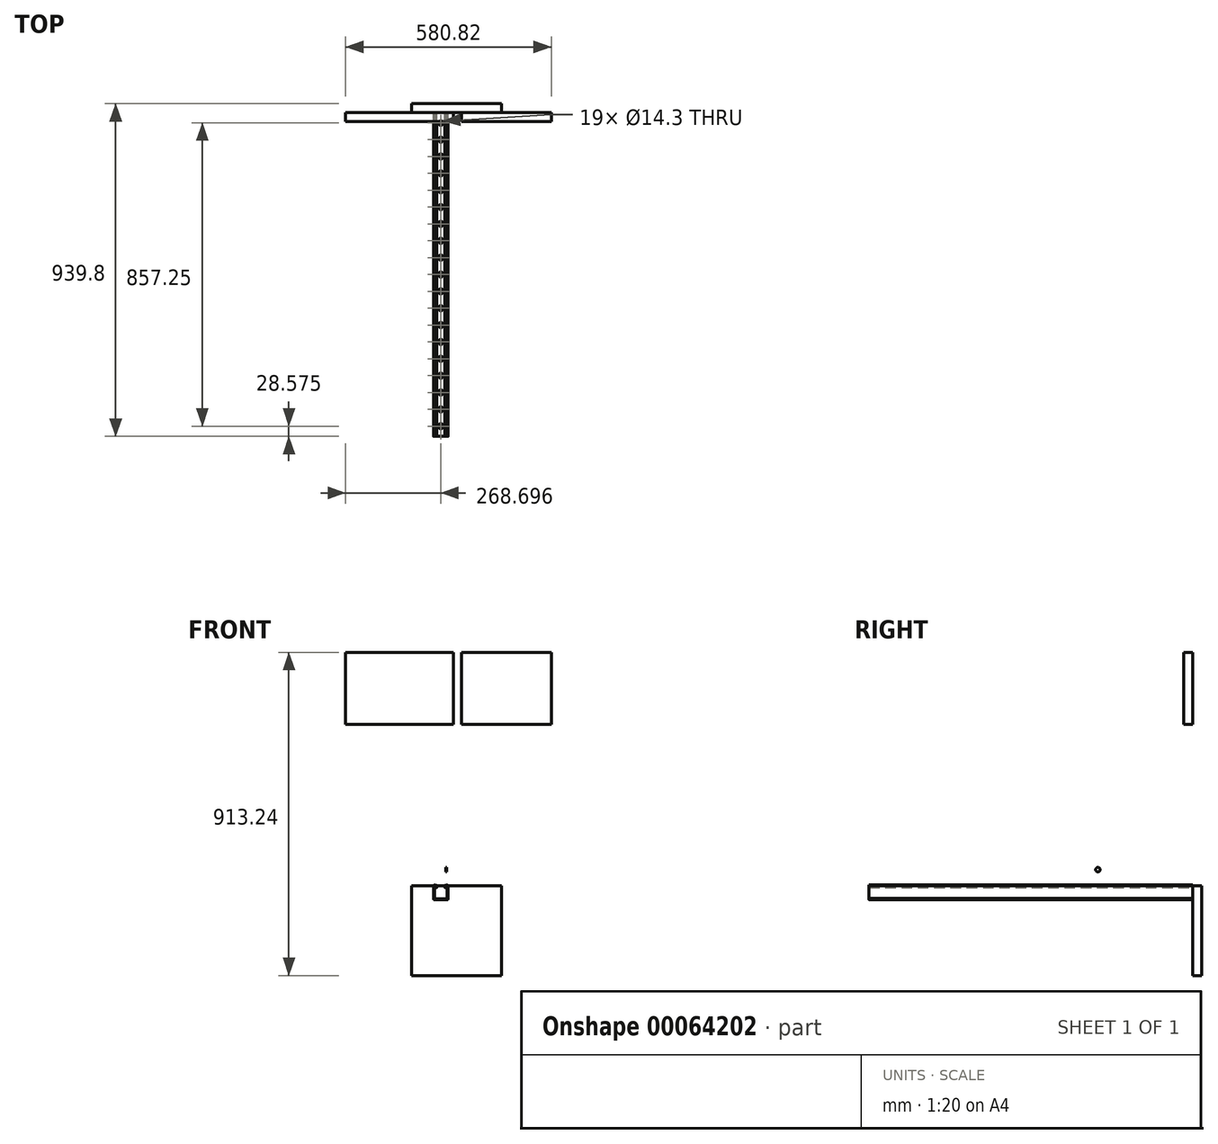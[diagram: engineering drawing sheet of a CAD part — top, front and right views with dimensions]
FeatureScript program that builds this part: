
annotation { "Feature Type Name" : "Feature", "Feature Type Description" : "" }
export const myFeature = defineFeature(function(context is Context, id is Id, definition is map)
    precondition{}
    {
        {
            var Q0;
            Q0=qCreatedBy(makeId("Front.planeOp"),FACE);
            var sketch = newSketch(context, id + "F0", { "sketchPlane" : qUnion([Q0])});
            skLineSegment(sketch, "E0.0", {"start": v(-47.01, 34.8) * mm, "end": v(-47.01, 32.45) * mm});
            skFitSpline(sketch, "E0.1", {"points": [v(-47.01, 32.45) * mm, v(-47.01, 31.71) * mm, v(-46.41, 31.12) * mm, v(-45.68, 31.12) * mm]});
            skFitSpline(sketch, "E0.2", {"points": [v(-45.68, 31.12) * mm, v(-44.94, 31.12) * mm, v(-44.34, 31.71) * mm, v(-44.34, 32.45) * mm]});
            skLineSegment(sketch, "E0.3", {"start": v(-44.34, 32.45) * mm, "end": v(-44.34, 34.8) * mm});
            skPoint(sketch, "E0.4", {"position": v(-43.55, 35.59) * mm});
            skPoint(sketch, "E0.5", {"position": v(-44.34, 34.8) * mm});
            skFitSpline(sketch, "E0.6", {"points": [v(-44.34, 34.8) * mm, v(-44.34, 35.23) * mm, v(-43.99, 35.59) * mm, v(-43.55, 35.59) * mm]});
            skPoint(sketch, "E0.7", {"position": v(-42.53, 35.59) * mm});
            skFitSpline(sketch, "E0.8", {"points": [v(-43.55, 38.25) * mm, v(-45.46, 38.25) * mm, v(-47.01, 36.7) * mm, v(-47.01, 34.8) * mm]});
            skLineSegment(sketch, "E0.9", {"start": v(-42.53, 38.25) * mm, "end": v(-43.55, 38.25) * mm});
            skFitSpline(sketch, "E0.10", {"points": [v(-37.49, 33.2) * mm, v(-37.49, 36) * mm, v(-39.75, 38.25) * mm, v(-42.53, 38.25) * mm]});
            skLineSegment(sketch, "E0.11", {"start": v(-37.49, 0.44) * mm, "end": v(-37.49, 33.2) * mm});
            skLineSegment(sketch, "E0.12", {"start": v(-40.15, 33.2) * mm, "end": v(-40.15, 0.44) * mm});
            skFitSpline(sketch, "E0.13", {"points": [v(-42.53, 35.59) * mm, v(-41.22, 35.59) * mm, v(-40.15, 34.52) * mm, v(-40.15, 33.2) * mm]});
            skLineSegment(sketch, "E0.14", {"start": v(-43.55, 35.59) * mm, "end": v(-42.53, 35.59) * mm});
            skFitSpline(sketch, "E0.15", {"points": [v(-40.15, 0.44) * mm, v(-40.15, 0) * mm, v(-40.5, -0.36) * mm, v(-40.95, -0.36) * mm]});
            skFitSpline(sketch, "E0.16", {"points": [v(-40.95, -3.02) * mm, v(-39.04, -3.02) * mm, v(-37.49, -1.47) * mm, v(-37.49, 0.44) * mm]});
            skLineSegment(sketch, "E0.17", {"start": v(-40.95, -0.36) * mm, "end": v(-75.3, -0.36) * mm});
            skLineSegment(sketch, "E0.18", {"start": v(-40.95, -3.02) * mm, "end": v(-75.3, -3.02) * mm});
            skFitSpline(sketch, "E0.19", {"points": [v(-75.3, -0.36) * mm, v(-75.74, -0.36) * mm, v(-76.1, 0) * mm, v(-76.1, 0.44) * mm]});
            skFitSpline(sketch, "E0.20", {"points": [v(-78.76, 0.44) * mm, v(-78.76, -1.47) * mm, v(-77.21, -3.02) * mm, v(-75.3, -3.02) * mm]});
            skLineSegment(sketch, "E0.21", {"start": v(-78.76, 33.2) * mm, "end": v(-78.76, 0.44) * mm});
            skLineSegment(sketch, "E0.22", {"start": v(-76.1, 0.44) * mm, "end": v(-76.1, 33.2) * mm});
            skFitSpline(sketch, "E0.23", {"points": [v(-73.71, 38.25) * mm, v(-76.5, 38.25) * mm, v(-78.76, 36) * mm, v(-78.76, 33.2) * mm]});
            skFitSpline(sketch, "E0.24", {"points": [v(-76.1, 33.2) * mm, v(-76.1, 34.52) * mm, v(-75.03, 35.59) * mm, v(-73.71, 35.59) * mm]});
            skLineSegment(sketch, "E0.25", {"start": v(-73.71, 35.59) * mm, "end": v(-72.7, 35.59) * mm});
            skLineSegment(sketch, "E0.26", {"start": v(-72.7, 38.25) * mm, "end": v(-73.71, 38.25) * mm});
            skFitSpline(sketch, "E0.27", {"points": [v(-69.24, 34.8) * mm, v(-69.24, 36.7) * mm, v(-70.79, 38.25) * mm, v(-72.7, 38.25) * mm]});
            skLineSegment(sketch, "E0.28", {"start": v(-69.24, 32.45) * mm, "end": v(-69.24, 34.8) * mm});
            skFitSpline(sketch, "E0.29", {"points": [v(-70.57, 31.12) * mm, v(-69.83, 31.12) * mm, v(-69.24, 31.71) * mm, v(-69.24, 32.45) * mm]});
            skFitSpline(sketch, "E0.30", {"points": [v(-71.9, 32.45) * mm, v(-71.9, 31.71) * mm, v(-71.3, 31.12) * mm, v(-70.57, 31.12) * mm]});
            skLineSegment(sketch, "E0.31", {"start": v(-71.9, 34.8) * mm, "end": v(-71.9, 32.45) * mm});
            skFitSpline(sketch, "E0.32", {"points": [v(-72.7, 35.59) * mm, v(-72.26, 35.59) * mm, v(-71.9, 35.23) * mm, v(-71.9, 34.8) * mm]});
            skLineSegment(sketch, "E1", {"start": v(-43.55, 38.25) * mm, "end": v(-72.7, 38.25) * mm});
            skLineSegment(sketch, "E2", {"start": v(-37.49, 33.2) * mm, "end": v(-37.49, 41.14) * mm});
            skLineSegment(sketch, "E3", {"start": v(-37.49, 41.14) * mm, "end": v(-78.76, 41.14) * mm});
            skLineSegment(sketch, "E4", {"start": v(-78.76, 41.14) * mm, "end": v(-78.76, 33.2) * mm});
            skLineSegment(sketch, "E5", {"start": v(-47.01, 34.8) * mm, "end": v(-69.24, 34.8) * mm});
            skSolve(sketch);
        }
        {
            var Q0;
            Q0=makeQuery(id+"F0.imprint","IMPRINT",FACE,{"disambiguationData":[TD([[makeQuery(id+"F0.imprint","IMPRINT",EDGE,{"derivedFrom":sQuery(id+"F0.wireOp",EDGE,"E0.0")}),1.0]])]});
            extrude(context, id + "F1", {"entities" : qUnion([Q0]), "depth" : 914.4 * mm});
        }
        {
            var Q0;
            Q0=makeQuery(id+"F1.opExtrude","SWEPT_FACE",FACE,{"disambiguationData":[OSD([sQuery(id+"F0.wireOp",EDGE,"E0.18")])]});
            var sketch = newSketch(context, id + "F2", { "sketchPlane" : qUnion([Q0])});
            skLineSegment(sketch, "E6.1", {"start": v(-75.3, 914.4) * mm, "end": v(-75.3, 0) * mm});
            skLineSegment(sketch, "E6.2", {"start": v(-40.95, 914.4) * mm, "end": v(-40.95, 0) * mm});
            skLineSegment(sketch, "E6.3", {"start": v(-40.95, 914.4) * mm, "end": v(-75.3, 914.4) * mm});
            skCircle(sketch, "E7", {"center": v(-58.12, 457.2) * mm, "radius": 6.35 * mm});
            skLineSegment(sketch, "E8", {"start": v(-75.3, 457.2) * mm, "end": v(-40.95, 458.5) * mm, "construction": true});
            skCircle(sketch, "E9.0.1.0", {"center": v(-58.12, 504.83) * mm, "radius": 6.35 * mm});
            skCircle(sketch, "E9.0.2.0", {"center": v(-58.12, 552.45) * mm, "radius": 6.35 * mm});
            skCircle(sketch, "E9.0.3.0", {"center": v(-58.12, 600.08) * mm, "radius": 6.35 * mm});
            skCircle(sketch, "E9.0.4.0", {"center": v(-58.12, 647.7) * mm, "radius": 6.35 * mm});
            skCircle(sketch, "E9.0.5.0", {"center": v(-58.12, 695.33) * mm, "radius": 6.35 * mm});
            skCircle(sketch, "E9.0.6.0", {"center": v(-58.12, 742.95) * mm, "radius": 6.35 * mm});
            skCircle(sketch, "E9.0.7.0", {"center": v(-58.12, 790.58) * mm, "radius": 6.35 * mm});
            skCircle(sketch, "E9.0.8.0", {"center": v(-58.12, 838.2) * mm, "radius": 6.35 * mm});
            skCircle(sketch, "E9.0.9.0", {"center": v(-58.12, 885.83) * mm, "radius": 6.35 * mm});
            skLineSegment(sketch, "E9.direction1", {"start": v(-58.12, 457.2) * mm, "end": v(-32.72, 457.2) * mm, "construction": true});
            skLineSegment(sketch, "E9.direction2", {"start": v(-58.12, 457.2) * mm, "end": v(-58.12, 504.83) * mm, "construction": true});
            skCircle(sketch, "E10.0.1.0", {"center": v(-58.12, 409.58) * mm, "radius": 6.35 * mm});
            skCircle(sketch, "E10.0.2.0", {"center": v(-58.12, 361.95) * mm, "radius": 6.35 * mm});
            skCircle(sketch, "E10.0.3.0", {"center": v(-58.12, 314.33) * mm, "radius": 6.35 * mm});
            skCircle(sketch, "E10.0.4.0", {"center": v(-58.12, 266.7) * mm, "radius": 6.35 * mm});
            skCircle(sketch, "E10.0.5.0", {"center": v(-58.12, 219.08) * mm, "radius": 6.35 * mm});
            skCircle(sketch, "E10.0.6.0", {"center": v(-58.12, 171.45) * mm, "radius": 6.35 * mm});
            skCircle(sketch, "E10.0.7.0", {"center": v(-58.12, 123.83) * mm, "radius": 6.35 * mm});
            skCircle(sketch, "E10.0.8.0", {"center": v(-58.12, 76.2) * mm, "radius": 6.35 * mm});
            skCircle(sketch, "E10.0.9.0", {"center": v(-58.12, 28.58) * mm, "radius": 6.35 * mm});
            skLineSegment(sketch, "E10.direction2", {"start": v(-58.12, 457.2) * mm, "end": v(-58.12, 409.58) * mm, "construction": true});
            skSolve(sketch);
        }
        {
            var Q0;
            Q0=sQuery(id+"F2.wireOp",VERTEX,"E9.0.9.0.center");
            var Q1;
            Q1=sQuery(id+"F2.wireOp",VERTEX,"E9.0.8.0.center");
            var Q2;
            Q2=sQuery(id+"F2.wireOp",VERTEX,"E9.0.7.0.center");
            var Q3;
            Q3=sQuery(id+"F2.wireOp",VERTEX,"E9.0.6.0.center");
            var Q4;
            Q4=sQuery(id+"F2.wireOp",VERTEX,"E9.0.5.0.center");
            var Q5;
            Q5=sQuery(id+"F2.wireOp",VERTEX,"E9.0.4.0.center");
            var Q6;
            Q6=sQuery(id+"F2.wireOp",VERTEX,"E9.0.3.0.center");
            var Q7;
            Q7=sQuery(id+"F2.wireOp",VERTEX,"E9.0.2.0.center");
            var Q8;
            Q8=sQuery(id+"F2.wireOp",VERTEX,"E9.direction2.end");
            var Q9;
            Q9=sQuery(id+"F2.wireOp",VERTEX,"E7.center");
            var Q10;
            Q10=sQuery(id+"F2.wireOp",VERTEX,"E10.0.1.0.center");
            var Q11;
            Q11=sQuery(id+"F2.wireOp",VERTEX,"E10.0.2.0.center");
            var Q12;
            Q12=sQuery(id+"F2.wireOp",VERTEX,"E10.0.3.0.center");
            var Q13;
            Q13=sQuery(id+"F2.wireOp",VERTEX,"E10.0.4.0.center");
            var Q14;
            Q14=sQuery(id+"F2.wireOp",VERTEX,"E10.0.5.0.center");
            var Q15;
            Q15=sQuery(id+"F2.wireOp",VERTEX,"E10.0.6.0.center");
            var Q16;
            Q16=sQuery(id+"F2.wireOp",VERTEX,"E10.0.7.0.center");
            var Q17;
            Q17=sQuery(id+"F2.wireOp",VERTEX,"E10.0.8.0.center");
            var Q18;
            Q18=sQuery(id+"F2.wireOp",VERTEX,"E10.0.9.0.center");
            var Q19;
            Q19=makeQuery(id+"F1.opExtrude","SWEPT_BODY",BODY,{"disambiguationData":[OSD([sQuery(id+"F0.wireOp",EDGE,"E0.0"),sQuery(id+"F0.wireOp",EDGE,"E0.1"),sQuery(id+"F0.wireOp",EDGE,"E0.2"),sQuery(id+"F0.wireOp",EDGE,"E0.3"),sQuery(id+"F0.wireOp",EDGE,"E0.6"),sQuery(id+"F0.wireOp",EDGE,"E0.8"),sQuery(id+"F0.wireOp",EDGE,"E0.9"),sQuery(id+"F0.wireOp",EDGE,"E0.10"),sQuery(id+"F0.wireOp",EDGE,"E0.11"),sQuery(id+"F0.wireOp",EDGE,"E0.12"),sQuery(id+"F0.wireOp",EDGE,"E0.13"),sQuery(id+"F0.wireOp",EDGE,"E0.14"),sQuery(id+"F0.wireOp",EDGE,"E0.15"),sQuery(id+"F0.wireOp",EDGE,"E0.16"),sQuery(id+"F0.wireOp",EDGE,"E0.17"),sQuery(id+"F0.wireOp",EDGE,"E0.18"),sQuery(id+"F0.wireOp",EDGE,"E0.19"),sQuery(id+"F0.wireOp",EDGE,"E0.20"),sQuery(id+"F0.wireOp",EDGE,"E0.21"),sQuery(id+"F0.wireOp",EDGE,"E0.22"),sQuery(id+"F0.wireOp",EDGE,"E0.23"),sQuery(id+"F0.wireOp",EDGE,"E0.24"),sQuery(id+"F0.wireOp",EDGE,"E0.25"),sQuery(id+"F0.wireOp",EDGE,"E0.26"),sQuery(id+"F0.wireOp",EDGE,"E0.27"),sQuery(id+"F0.wireOp",EDGE,"E0.28"),sQuery(id+"F0.wireOp",EDGE,"E0.29"),sQuery(id+"F0.wireOp",EDGE,"E0.30"),sQuery(id+"F0.wireOp",EDGE,"E0.31"),sQuery(id+"F0.wireOp",EDGE,"E0.32")])]});
            hole(context, id + "F3", {"style" : HoleStyle.SIMPLE, "holeDiameter" : 14.3 * mm, "endStyle" : HoleEndStyle.THROUGH, "locations" : qUnion([Q0, Q1, Q2, Q3, Q4, Q5, Q6, Q7, Q8, Q9, Q10, Q11, Q12, Q13, Q14, Q15, Q16, Q17, Q18]), "scope" : qUnion([Q19])});
        }
        {
            var Q0;
            Q0=qCreatedBy(makeId("Front.planeOp"),FACE);
            var sketch = newSketch(context, id + "F4", { "sketchPlane" : qUnion([Q0])});
            skLineSegment(sketch, "E11.bottom", {"start": v(-140.58, 36.99) * mm, "end": v(113.42, 36.99) * mm});
            skLineSegment(sketch, "E11.top", {"start": v(-140.58, -217.01) * mm, "end": v(113.42, -217.01) * mm});
            skLineSegment(sketch, "E11.left", {"start": v(-140.58, 36.99) * mm, "end": v(-140.58, -217.01) * mm});
            skLineSegment(sketch, "E11.right", {"start": v(113.42, 36.99) * mm, "end": v(113.42, -217.01) * mm});
            skLineSegment(sketch, "E12", {"start": v(-140.58, 36.99) * mm, "end": v(113.42, -217.01) * mm, "construction": true});
            skLineSegment(sketch, "E13", {"start": v(113.42, 36.99) * mm, "end": v(-140.58, -217.01) * mm, "construction": true});
            skLineSegment(sketch, "E14", {"start": v(-140.58, -90.01) * mm, "end": v(113.42, -90.01) * mm, "construction": true});
            skLineSegment(sketch, "E15", {"start": v(113.42, -90.01) * mm, "end": v(-13.58, -217.01) * mm, "construction": true});
            skLineSegment(sketch, "E16", {"start": v(-13.58, -217.01) * mm, "end": v(-13.58, 36.99) * mm, "construction": true});
            skLineSegment(sketch, "E17", {"start": v(-13.58, 36.99) * mm, "end": v(-140.58, -90.01) * mm, "construction": true});
            skLineSegment(sketch, "E18", {"start": v(-77.08, -26.51) * mm, "end": v(-77.08, 36.99) * mm, "construction": true});
            skLineSegment(sketch, "E19", {"start": v(-77.08, 36.99) * mm, "end": v(-140.58, -26.51) * mm, "construction": true});
            skLineSegment(sketch, "E20", {"start": v(-140.58, -26.51) * mm, "end": v(-108.83, 5.24) * mm, "construction": true});
            skSolve(sketch);
        }
        {
            var Q0;
            Q0=makeQuery(id+"F4.imprint","IMPRINT",FACE,{"disambiguationData":[TD([[makeQuery(id+"F4.imprint","IMPRINT",EDGE,{"derivedFrom":sQuery(id+"F4.wireOp",EDGE,"E11.bottom")}),-1.0]])]});
            extrude(context, id + "F5", {"entities" : qUnion([Q0]), "oppositeDirection" : true, "depth" : 25.4 * mm});
        }
        {
            var Q0;
            Q0=qCreatedBy(makeId("Front.planeOp"),FACE);
            var sketch = newSketch(context, id + "F6", { "sketchPlane" : qUnion([Q0])});
            skLineSegment(sketch, "E21.bottom", {"start": v(0, 696.23) * mm, "end": v(254, 696.23) * mm});
            skLineSegment(sketch, "E21.top", {"start": v(0, 493.03) * mm, "end": v(254, 493.03) * mm});
            skLineSegment(sketch, "E21.left", {"start": v(0, 696.23) * mm, "end": v(0, 493.03) * mm});
            skLineSegment(sketch, "E21.right", {"start": v(254, 696.23) * mm, "end": v(254, 493.03) * mm});
            skLineSegment(sketch, "E22.bottom", {"start": v(-22.02, 696.23) * mm, "end": v(-326.82, 696.23) * mm});
            skLineSegment(sketch, "E22.top", {"start": v(-22.02, 493.03) * mm, "end": v(-326.82, 493.03) * mm});
            skLineSegment(sketch, "E22.left", {"start": v(-22.02, 696.23) * mm, "end": v(-22.02, 493.03) * mm});
            skLineSegment(sketch, "E22.right", {"start": v(-326.82, 696.23) * mm, "end": v(-326.82, 493.03) * mm});
            skSolve(sketch);
        }
        {
            var Q0;
            Q0=makeQuery(id+"F6.imprint","IMPRINT",FACE,{"disambiguationData":[TD([[makeQuery(id+"F6.imprint","IMPRINT",EDGE,{"derivedFrom":sQuery(id+"F6.wireOp",EDGE,"E22.bottom")}),1.0]])]});
            var Q1;
            Q1=makeQuery(id+"F6.imprint","IMPRINT",FACE,{"disambiguationData":[TD([[makeQuery(id+"F6.imprint","IMPRINT",EDGE,{"derivedFrom":sQuery(id+"F6.wireOp",EDGE,"E21.bottom")}),-1.0]])]});
            extrude(context, id + "F7", {"entities" : qUnion([Q0, Q1]), "depth" : 25.4 * mm});
        }
        {
            var Q0;
            Q0=qCreatedBy(makeId("Front.planeOp"),FACE);
            var sketch = newSketch(context, id + "F8", { "sketchPlane" : qUnion([Q0])});
            skLineSegment(sketch, "E23", {"start": v(6.42, 56.7) * mm, "end": v(-44.38, 56.7) * mm});
            skLineSegment(sketch, "E24", {"start": v(-44.38, 56.7) * mm, "end": v(-44.38, 107.5) * mm});
            skLineSegment(sketch, "E25", {"start": v(-44.38, 107.5) * mm, "end": v(-41.2, 107.5) * mm});
            skLineSegment(sketch, "E26", {"start": v(-41.2, 107.5) * mm, "end": v(-41.2, 59.87) * mm});
            skLineSegment(sketch, "E27", {"start": v(-41.2, 59.87) * mm, "end": v(6.42, 59.87) * mm});
            skLineSegment(sketch, "E28", {"start": v(6.42, 56.7) * mm, "end": v(6.42, 59.87) * mm});
            skSolve(sketch);
        }
        {
            var Q0;
            Q0=makeQuery(id+"F8.imprint","IMPRINT",FACE,{"disambiguationData":[TD([[makeQuery(id+"F8.imprint","IMPRINT",EDGE,{"derivedFrom":sQuery(id+"F8.wireOp",EDGE,"E23")}),-1.0]])]});
            extrude(context, id + "F9", {"entities" : qUnion([Q0]), "depth" : 304.8 * mm});
        }
        {
            var Q0;
            Q0=makeQuery(id+"F9.opExtrude","SWEPT_FACE",FACE,{"disambiguationData":[OSD([sQuery(id+"F8.wireOp",EDGE,"E24")])]});
            var sketch = newSketch(context, id + "F10", { "sketchPlane" : qUnion([Q0])});
            skLineSegment(sketch, "E29.0", {"start": v(304.8, 107.5) * mm, "end": v(0, 107.5) * mm});
            skLineSegment(sketch, "E29.1", {"start": v(0, 56.7) * mm, "end": v(0, 107.5) * mm});
            skLineSegment(sketch, "E29.2", {"start": v(304.8, 56.7) * mm, "end": v(0, 56.7) * mm});
            skLineSegment(sketch, "E29.3", {"start": v(304.8, 56.7) * mm, "end": v(304.8, 107.5) * mm});
            skLineSegment(sketch, "E30", {"start": v(152.4, 107.5) * mm, "end": v(152.4, 56.7) * mm, "construction": true});
            skLineSegment(sketch, "E31", {"start": v(0, 107.5) * mm, "end": v(37.03, 82.1) * mm, "construction": true});
            skLineSegment(sketch, "E32", {"start": v(37.03, 82.1) * mm, "end": v(0, 56.7) * mm, "construction": true});
            skCircle(sketch, "E33", {"center": v(37.03, 82.1) * mm, "radius": 6.35 * mm});
            skCircle(sketch, "E34.MirrorC", {"center": v(267.77, 82.1) * mm, "radius": 6.35 * mm});
            skSolve(sketch);
        }
        {
            var Q0;
            Q0=makeQuery(id+"F10.imprint","IMPRINT",FACE,{"disambiguationData":[TD([[makeQuery(id+"F10.imprint","IMPRINT",EDGE,{"derivedFrom":sQuery(id+"F10.wireOp",EDGE,"E33")}),1.0]])]});
            var Q1;
            Q1=makeQuery(id+"F10.imprint","IMPRINT",FACE,{"disambiguationData":[TD([[makeQuery(id+"F10.imprint","IMPRINT",EDGE,{"derivedFrom":sQuery(id+"F10.wireOp",EDGE,"E34.MirrorC")}),-1.0]])]});
            extrude(context, id + "F11", {"entities" : qUnion([Q0, Q1]), "operationType" : NewBodyOperationType.REMOVE, "endBound" : BoundingType.THROUGH_ALL, "oppositeDirection" : true, "depth" : 25.4 * mm});
        }
    });
